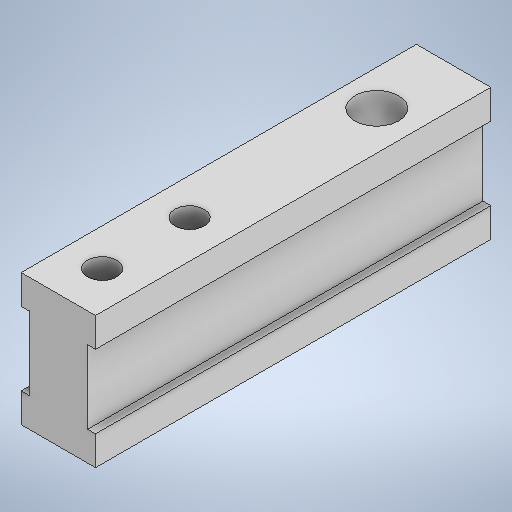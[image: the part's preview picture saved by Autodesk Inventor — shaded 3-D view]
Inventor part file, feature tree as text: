
AUTODESK INVENTOR PART (.ipt)
format: ipt  version: 2025.1 (Build 291241000, 241)  size: 594,944 bytes
history: native  units: in
note: dims shown in document units (in); Inventor stores cm internally (conversion verified against a paired STEP export)
features: extrude x3, sketch x3
ambient origin geometry x8: Origin, YZ Plane, XZ Plane, XY Plane, X Axis, Y Axis, Z Axis, Center Point
bodies: Solid1 (feature_tree)
feature tree (6):
  extrude  "Extrusion1"  Depth=1.063in
  extrude  "Extrusion2"  Depth=1.063in TaperAngle=0.0deg
  extrude  "Extrusion3"  Depth=0.0787in
  sketch  "Sketch1"  dims[d0=1.063in d1=0.0in d2=0.8606in]
  sketch  "Sketch2"  dims[d3=0.1181in d4=1.063in d5=0.0in]
  sketch  "Sketch3"  dims[d6=0.0787in d7=0.0787in d8=0.1181in d9=0.3543in d10=0.2in d11=1.063in d12=0.0in]
